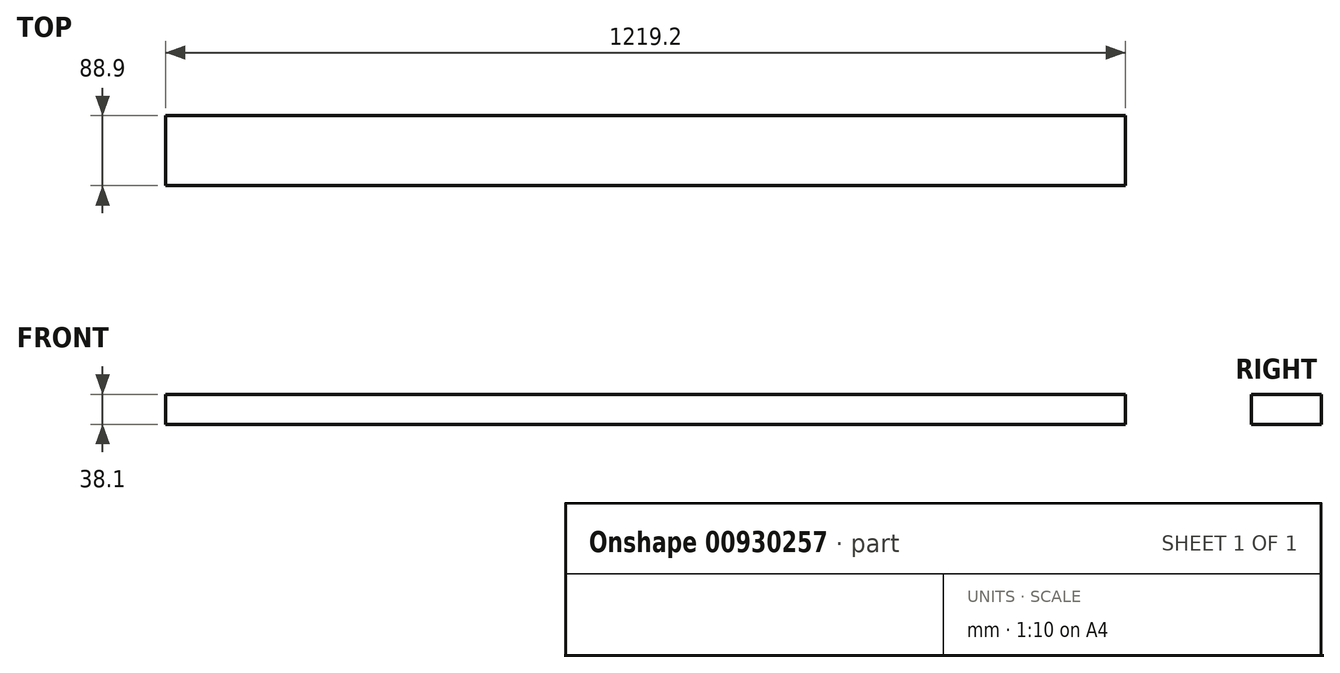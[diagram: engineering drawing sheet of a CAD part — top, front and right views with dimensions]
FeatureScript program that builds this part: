
annotation { "Feature Type Name" : "Feature", "Feature Type Description" : "" }
export const myFeature = defineFeature(function(context is Context, id is Id, definition is map)
    precondition{}
    {
        {
            var Q0;
            Q0=qCreatedBy(makeId("Right.planeOp"),FACE);
            var sketch = newSketch(context, id + "F0", { "sketchPlane" : qUnion([Q0])});
            skLineSegment(sketch, "E0.bottom", {"start": v(44.45, -19.05) * mm, "end": v(-44.45, -19.05) * mm});
            skLineSegment(sketch, "E0.top", {"start": v(44.45, 19.05) * mm, "end": v(-44.45, 19.05) * mm});
            skLineSegment(sketch, "E0.left", {"start": v(44.45, -19.05) * mm, "end": v(44.45, 19.05) * mm});
            skLineSegment(sketch, "E0.right", {"start": v(-44.45, -19.05) * mm, "end": v(-44.45, 19.05) * mm});
            skPoint(sketch, "E0.middle", {"position": v(0, 0) * mm});
            skSolve(sketch);
        }
        {
            var Q0;
            Q0=qSketchRegion(id+"F0",true);
            extrude(context, id + "F1", {"entities" : qUnion([Q0]), "endBound" : BoundingType.SYMMETRIC, "depth" : 1219.2 * mm});
        }
    });
